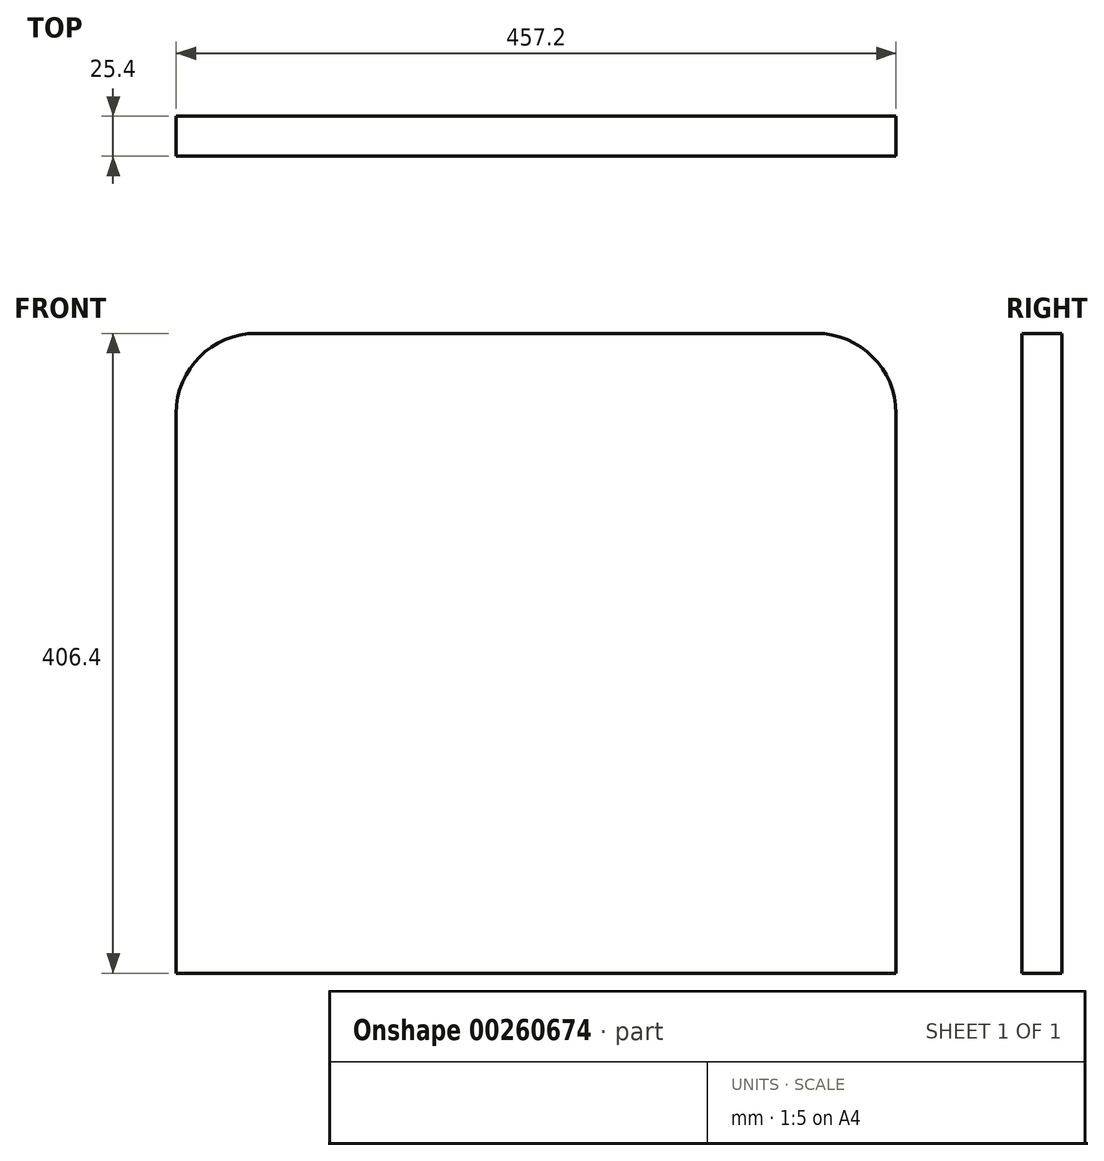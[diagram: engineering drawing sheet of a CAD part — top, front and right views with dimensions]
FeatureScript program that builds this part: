
annotation { "Feature Type Name" : "Feature", "Feature Type Description" : "" }
export const myFeature = defineFeature(function(context is Context, id is Id, definition is map)
    precondition{}
    {
        {
            var Q0;
            Q0=qCreatedBy(makeId("Front.planeOp"),FACE);
            var sketch = newSketch(context, id + "F0", { "sketchPlane" : qUnion([Q0])});
            skLineSegment(sketch, "E0.bottom", {"start": v(-132.37, 233.13) * mm, "end": v(223.23, 233.13) * mm});
            skLineSegment(sketch, "E0.top", {"start": v(-183.17, -173.27) * mm, "end": v(274.03, -173.27) * mm});
            skLineSegment(sketch, "E0.left", {"start": v(-183.17, 182.33) * mm, "end": v(-183.17, -173.27) * mm});
            skLineSegment(sketch, "E0.right", {"start": v(274.03, 182.33) * mm, "end": v(274.03, -173.27) * mm});
            skPoint(sketch, "E1.visualSharp", {"position": v(-183.17, 233.13) * mm});
            skArc(sketch, "E1.filletArc", {"start": v(-132.37, 233.13) * mm, "mid": v(-168.29, 218.25) * mm, "end": v(-183.17, 182.33) * mm});
            skPoint(sketch, "E2.visualSharp", {"position": v(274.03, 233.13) * mm});
            skArc(sketch, "E2.filletArc", {"start": v(274.03, 182.33) * mm, "mid": v(259.15, 218.25) * mm, "end": v(223.23, 233.13) * mm});
            skSolve(sketch);
        }
        {
            var Q0;
            Q0=makeQuery(id+"F0.imprint","IMPRINT",FACE,{"disambiguationData":[TD([[makeQuery(id+"F0.imprint","IMPRINT",EDGE,{"derivedFrom":sQuery(id+"F0.wireOp",EDGE,"E0.bottom")}),-1.0]])]});
            extrude(context, id + "F1", {"entities" : qUnion([Q0]), "depth" : 25.4 * mm});
        }
    });
